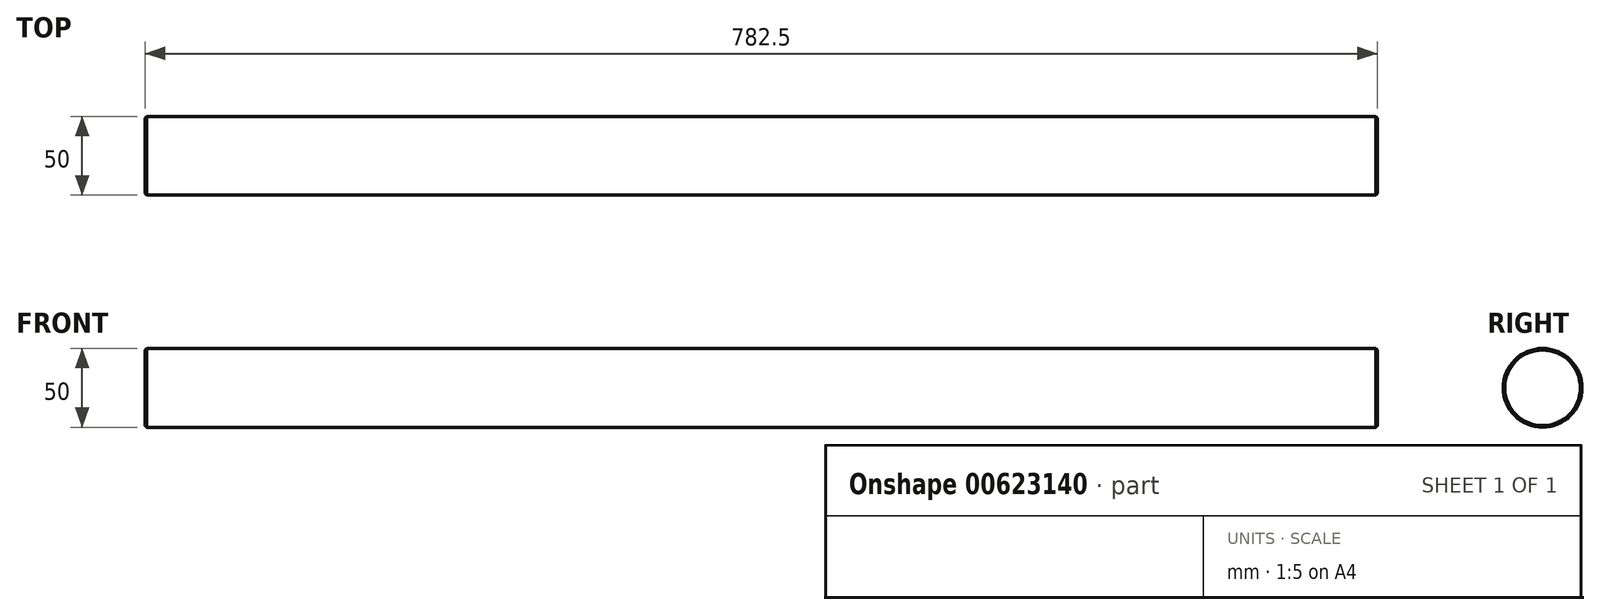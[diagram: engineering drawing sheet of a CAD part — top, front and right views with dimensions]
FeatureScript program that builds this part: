
annotation { "Feature Type Name" : "Feature", "Feature Type Description" : "" }
export const myFeature = defineFeature(function(context is Context, id is Id, definition is map)
    precondition{}
    {
        {
            var Q0;
            Q0=qCreatedBy(makeId("Right.planeOp"),FACE);
            var sketch = newSketch(context, id + "F0", { "sketchPlane" : qUnion([Q0])});
            skCircle(sketch, "E0", {"center": v(0, 0) * mm, "radius": 25 * mm});
            skSolve(sketch);
        }
        {
            var Q0;
            Q0 = qSketchRegion(id + "F0", true);
            extrude(context, id + "F1", {"entities" : qUnion([Q0]), "depth" : 782.5 * mm, "offsetDistance" : 25 * mm});
        }
        {
            var Q0;
            Q0=makeQuery(id+"F1.opExtrude","CAP_EDGE",EDGE,{"disambiguationData":[OSD([sQuery(id+"F0.wireOp",EDGE,"E0")])],"isStart":false});
            var Q1;
            Q1=makeQuery(id+"F1.opExtrude","CAP_EDGE",EDGE,{"disambiguationData":[OSD([sQuery(id+"F0.wireOp",EDGE,"E0")])],"isStart":true});
            chamfer(context, id + "F2", {"entities" : qUnion([Q0, Q1]), "width" : 1 * mm, "tangentPropagation" : true});
        }
    });
